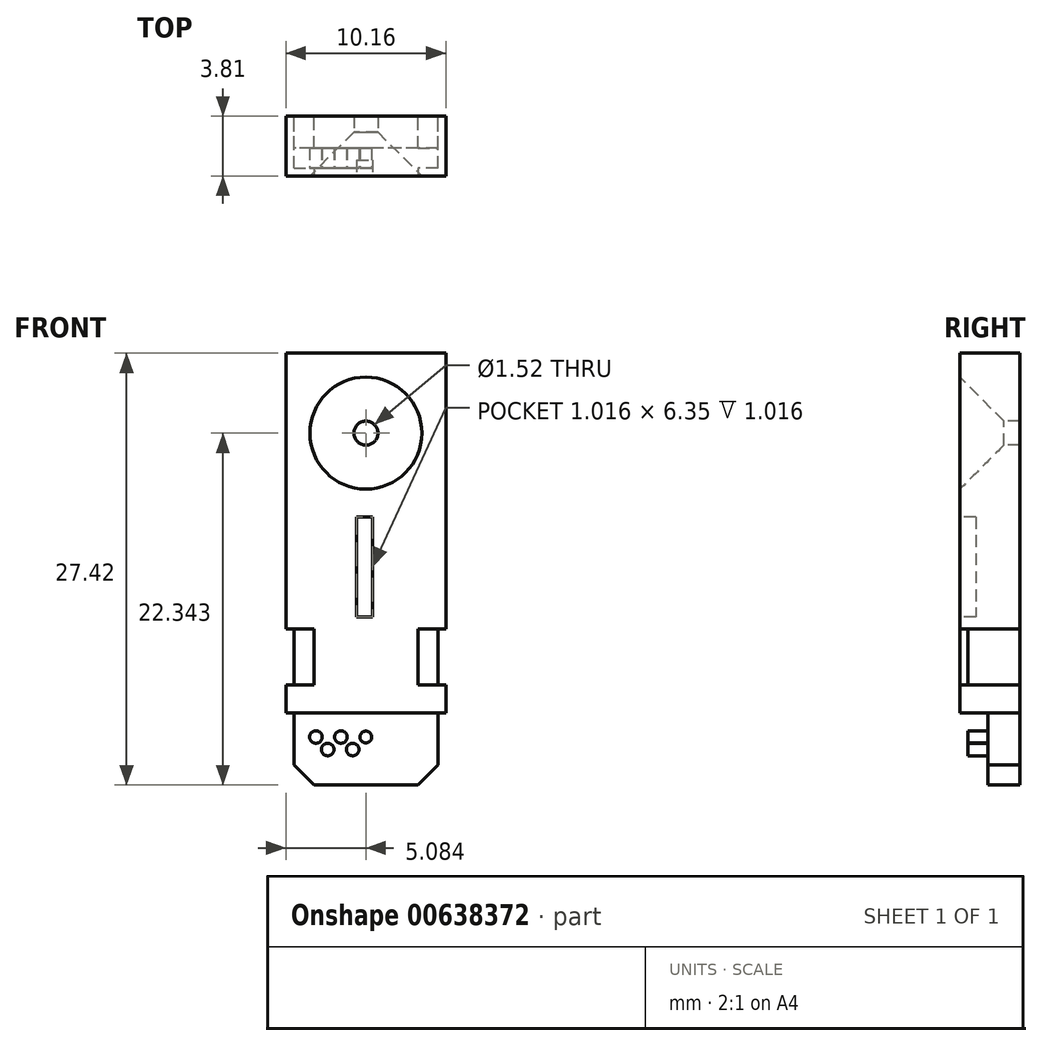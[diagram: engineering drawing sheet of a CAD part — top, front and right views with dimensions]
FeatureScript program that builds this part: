
annotation { "Feature Type Name" : "Feature", "Feature Type Description" : "" }
export const myFeature = defineFeature(function(context is Context, id is Id, definition is map)
    precondition{}
    {
        {
            var Q0;
            Q0=qCreatedBy(makeId("Front.planeOp"),FACE);
            var sketch = newSketch(context, id + "F0", { "sketchPlane" : qUnion([Q0])});
            skLineSegment(sketch, "E0", {"start": v(11.18, 15.01) * mm, "end": v(21.34, 15.01) * mm});
            skLineSegment(sketch, "E1", {"start": v(21.34, 15.01) * mm, "end": v(21.34, -7.85) * mm});
            skLineSegment(sketch, "E2", {"start": v(21.34, -7.85) * mm, "end": v(20.84, -7.85) * mm});
            skLineSegment(sketch, "E3", {"start": v(11.18, -7.85) * mm, "end": v(11.18, 15.01) * mm});
            skLineSegment(sketch, "E4", {"start": v(11.18, -7.85) * mm, "end": v(11.7, -7.85) * mm});
            skLineSegment(sketch, "E5", {"start": v(11.7, -7.85) * mm, "end": v(11.7, -11.14) * mm});
            skLineSegment(sketch, "E6", {"start": v(12.96, -12.41) * mm, "end": v(11.7, -11.14) * mm});
            skLineSegment(sketch, "E7", {"start": v(20.84, -7.85) * mm, "end": v(20.84, -11.14) * mm});
            skLineSegment(sketch, "E8", {"start": v(19.57, -12.41) * mm, "end": v(20.84, -11.14) * mm});
            skLineSegment(sketch, "E9", {"start": v(19.57, -12.41) * mm, "end": v(12.96, -12.41) * mm});
            skLineSegment(sketch, "E10", {"start": v(11.7, -7.85) * mm, "end": v(11.18, -7.85) * mm});
            skLineSegment(sketch, "E11", {"start": v(20.84, -7.85) * mm, "end": v(11.7, -7.85) * mm});
            skSolve(sketch);
        }
        {
            var Q0;
            Q0=makeQuery(id+"F0.imprint","IMPRINT",FACE,{"disambiguationData":[TD([[makeQuery(id+"F0.imprint","IMPRINT",EDGE,{"derivedFrom":sQuery(id+"F0.wireOp",EDGE,"E0")}),-1.0]])]});
            extrude(context, id + "F1", {"entities" : qUnion([Q0]), "depth" : 3.8 * mm, "offsetDistance" : 25.4 * mm});
        }
        {
            var Q0;
            Q0=makeQuery(id+"F0.imprint","IMPRINT",FACE,{"disambiguationData":[TD([[makeQuery(id+"F0.imprint","IMPRINT",EDGE,{"derivedFrom":sQuery(id+"F0.wireOp",EDGE,"E5")}),1.0]])]});
            extrude(context, id + "F2", {"entities" : qUnion([Q0]), "operationType" : NewBodyOperationType.ADD, "depth" : 3.3 * mm, "offsetDistance" : 25.4 * mm});
        }
        {
            var Q0;
            Q0=makeQuery(id+"F1.opExtrude","CAP_FACE",FACE,{"disambiguationData":[OSD([sQuery(id+"F0.wireOp",EDGE,"E0"),sQuery(id+"F0.wireOp",EDGE,"E1"),sQuery(id+"F0.wireOp",EDGE,"E3"),sQuery(id+"F0.wireOp",EDGE,"E2"),sQuery(id+"F0.wireOp",EDGE,"E10"),sQuery(id+"F0.wireOp",EDGE,"E11")])],"isStart":false});
            var sketch = newSketch(context, id + "F3", { "sketchPlane" : qUnion([Q0])});
            skLineSegment(sketch, "E12", {"start": v(16.26, 15.01) * mm, "end": v(16.26, 9.93) * mm});
            skPoint(sketch, "E12.endSnap0", {"position": v(16.26, 15.01) * mm});
            skSolve(sketch);
        }
        {
            var Q0;
            Q0=sQuery(id+"F3.wireOp",VERTEX,"E12.end");
            var Q1;
            Q1=makeQuery(id+"F1.opExtrude","SWEPT_BODY",BODY,{"disambiguationData":[OSD([sQuery(id+"F0.wireOp",EDGE,"E0"),sQuery(id+"F0.wireOp",EDGE,"E1"),sQuery(id+"F0.wireOp",EDGE,"E3"),sQuery(id+"F0.wireOp",EDGE,"E2"),sQuery(id+"F0.wireOp",EDGE,"E10"),sQuery(id+"F0.wireOp",EDGE,"E11")])]});
            hole(context, id + "F4", {"style" : HoleStyle.C_SINK, "endStyle" : HoleEndStyle.THROUGH, "holeDiameter" : 1.52 * mm, "cSinkDiameter" : 7.11 * mm, "cSinkAngle" : 90 * degree, "majorDiameter" : 6.35 * mm, "isTappedThrough" : true, "tappedDepth" : 12.7 * mm, "tapClearance" : 3, "startFromSketch" : true, "locations" : qUnion([Q0]), "scope" : qUnion([Q1])});
        }
        {
            var Q0;
            Q0=makeQuery(id+"F1.opExtrude","CAP_FACE",FACE,{"disambiguationData":[OSD([sQuery(id+"F0.wireOp",EDGE,"E0"),sQuery(id+"F0.wireOp",EDGE,"E1"),sQuery(id+"F0.wireOp",EDGE,"E3"),sQuery(id+"F0.wireOp",EDGE,"E2"),sQuery(id+"F0.wireOp",EDGE,"E10"),sQuery(id+"F0.wireOp",EDGE,"E11")])],"isStart":false});
            var sketch = newSketch(context, id + "F5", { "sketchPlane" : qUnion([Q0])});
            skLineSegment(sketch, "E13", {"start": v(16.19, 4.6) * mm, "end": v(16.7, 4.6) * mm});
            skLineSegment(sketch, "E14", {"start": v(16.7, 4.6) * mm, "end": v(15.68, 4.6) * mm});
            skLineSegment(sketch, "E15", {"start": v(15.68, 4.6) * mm, "end": v(15.68, -1.75) * mm});
            skLineSegment(sketch, "E16", {"start": v(15.68, -1.75) * mm, "end": v(16.7, -1.75) * mm});
            skLineSegment(sketch, "E17", {"start": v(16.7, -1.75) * mm, "end": v(16.7, 4.6) * mm});
            skSolve(sketch);
        }
        {
            var Q0;
            {var subQ0=sQuery(id+"F5.wireOp",EDGE,"E15");Q0=makeQuery(id+"F5.imprint","IMPRINT",FACE,{"disambiguationData":[TD([[makeQuery(id+"F5.imprint","IMPRINT",EDGE,{"derivedFrom":subQ0}),1.0]])]});}
            extrude(context, id + "F6", {"entities" : qUnion([Q0]), "operationType" : NewBodyOperationType.REMOVE, "oppositeDirection" : true, "depth" : 1.02 * mm, "offsetDistance" : 25.4 * mm});
        }
        {
            var Q0;
            Q0=makeQuery(id+"F1.opExtrude","CAP_FACE",FACE,{"disambiguationData":[OSD([sQuery(id+"F0.wireOp",EDGE,"E0"),sQuery(id+"F0.wireOp",EDGE,"E1"),sQuery(id+"F0.wireOp",EDGE,"E3"),sQuery(id+"F0.wireOp",EDGE,"E2"),sQuery(id+"F0.wireOp",EDGE,"E10"),sQuery(id+"F0.wireOp",EDGE,"E11")])],"isStart":false});
            var sketch = newSketch(context, id + "F7", { "sketchPlane" : qUnion([Q0])});
            skLineSegment(sketch, "E18", {"start": v(11.18, -7.85) * mm, "end": v(11.18, -6.07) * mm});
            skLineSegment(sketch, "E19", {"start": v(11.18, -6.07) * mm, "end": v(12.96, -6.07) * mm});
            skLineSegment(sketch, "E20", {"start": v(12.96, -6.07) * mm, "end": v(12.96, -2.51) * mm});
            skLineSegment(sketch, "E21", {"start": v(12.96, -2.51) * mm, "end": v(11.18, -2.51) * mm});
            skLineSegment(sketch, "E22", {"start": v(21.34, -6.07) * mm, "end": v(19.57, -6.07) * mm});
            skLineSegment(sketch, "E23", {"start": v(19.57, -6.07) * mm, "end": v(19.57, -2.51) * mm});
            skLineSegment(sketch, "E24", {"start": v(19.57, -2.51) * mm, "end": v(21.34, -2.51) * mm});
            skSolve(sketch);
        }
        {
            var Q0;
            {var subQ0=sQuery(id+"F7.wireOp",EDGE,"E19");Q0=makeQuery(id+"F7.imprint","IMPRINT",FACE,{"disambiguationData":[TD([[makeQuery(id+"F7.imprint","IMPRINT",EDGE,{"derivedFrom":subQ0}),1.0]])]});}
            var Q1;
            {var subQ0=sQuery(id+"F7.wireOp",EDGE,"E22");Q1=makeQuery(id+"F7.imprint","IMPRINT",FACE,{"disambiguationData":[TD([[makeQuery(id+"F7.imprint","IMPRINT",EDGE,{"derivedFrom":subQ0}),-1.0]])]});}
            extrude(context, id + "F8", {"entities" : qUnion([Q0, Q1]), "operationType" : NewBodyOperationType.REMOVE, "oppositeDirection" : true, "depth" : 0.5 * mm, "offsetDistance" : 25.4 * mm});
        }
        {
            var Q0;
            Q0=makeQuery(id+"F1.opExtrude","SWEPT_FACE",FACE,{"disambiguationData":[OSD([sQuery(id+"F0.wireOp",EDGE,"E1")])]});
            var sketch = newSketch(context, id + "F9", { "sketchPlane" : qUnion([Q0])});
            skLineSegment(sketch, "E25", {"start": v(-3.3, -2.51) * mm, "end": v(0, -2.51) * mm});
            skLineSegment(sketch, "E26", {"start": v(-3.3, -6.07) * mm, "end": v(0, -6.07) * mm});
            skSolve(sketch);
        }
        {
            var Q0;
            {var subQ0=sQuery(id+"F9.wireOp",EDGE,"E25");Q0=makeQuery(id+"F9.imprint","IMPRINT",FACE,{"disambiguationData":[TD([[makeQuery(id+"F9.imprint","IMPRINT",EDGE,{"derivedFrom":subQ0}),-1.0]])]});}
            extrude(context, id + "F10", {"entities" : qUnion([Q0]), "operationType" : NewBodyOperationType.REMOVE, "oppositeDirection" : true, "depth" : 0.5 * mm, "offsetDistance" : 25.4 * mm});
        }
        {
            var Q0;
            Q0=makeQuery(id+"F1.opExtrude","SWEPT_FACE",FACE,{"disambiguationData":[OSD([sQuery(id+"F0.wireOp",EDGE,"E3")])]});
            var sketch = newSketch(context, id + "F11", { "sketchPlane" : qUnion([Q0])});
            skLineSegment(sketch, "E27", {"start": v(3.3, -2.51) * mm, "end": v(0, -2.51) * mm});
            skLineSegment(sketch, "E28", {"start": v(3.3, -6.07) * mm, "end": v(0, -6.07) * mm});
            skSolve(sketch);
        }
        {
            var Q0;
            {var subQ0=sQuery(id+"F11.wireOp",EDGE,"E27");Q0=makeQuery(id+"F11.imprint","IMPRINT",FACE,{"disambiguationData":[TD([[makeQuery(id+"F11.imprint","IMPRINT",EDGE,{"derivedFrom":subQ0}),1.0]])]});}
            extrude(context, id + "F12", {"entities" : qUnion([Q0]), "operationType" : NewBodyOperationType.REMOVE, "oppositeDirection" : true, "depth" : 0.5 * mm, "offsetDistance" : 25.4 * mm});
        }
        {
            var Q0;
            Q0=makeQuery(id+"F2.opExtrude","CAP_FACE",FACE,{"disambiguationData":[OSD([sQuery(id+"F0.wireOp",EDGE,"E5"),sQuery(id+"F0.wireOp",EDGE,"E6"),sQuery(id+"F0.wireOp",EDGE,"E7"),sQuery(id+"F0.wireOp",EDGE,"E8"),sQuery(id+"F0.wireOp",EDGE,"E9"),sQuery(id+"F0.wireOp",EDGE,"E11")])],"isStart":false});
            var sketch = newSketch(context, id + "F13", { "sketchPlane" : qUnion([Q0])});
            skCircle(sketch, "E29", {"center": v(16.26, -9.37) * mm, "radius": 0.37 * mm});
            skCircle(sketch, "E30", {"center": v(17.1, -10.17) * mm, "radius": 0.4 * mm});
            skCircle(sketch, "E31", {"center": v(17.85, -9.37) * mm, "radius": 0.4 * mm});
            skCircle(sketch, "E32", {"center": v(18.69, -10.17) * mm, "radius": 0.4 * mm});
            skCircle(sketch, "E33", {"center": v(19.44, -9.37) * mm, "radius": 0.4 * mm});
            skCircle(sketch, "E34.MirrorC", {"center": v(15.43, -10.17) * mm, "radius": 0.4 * mm});
            skCircle(sketch, "E35.MirrorC", {"center": v(14.68, -9.37) * mm, "radius": 0.4 * mm});
            skCircle(sketch, "E36.MirrorC", {"center": v(13.84, -10.17) * mm, "radius": 0.4 * mm});
            skCircle(sketch, "E37.MirrorC", {"center": v(13.09, -9.37) * mm, "radius": 0.4 * mm});
            skSolve(sketch);
        }
        {
            var Q0;
            Q0=makeQuery(id+"F13.imprint","IMPRINT",FACE,{"disambiguationData":[TD([[makeQuery(id+"F13.imprint","IMPRINT",EDGE,{"derivedFrom":sQuery(id+"F13.wireOp",EDGE,"E37.MirrorC")}),-1.0]])]});
            var Q1;
            Q1=makeQuery(id+"F13.imprint","IMPRINT",FACE,{"disambiguationData":[TD([[makeQuery(id+"F13.imprint","IMPRINT",EDGE,{"derivedFrom":sQuery(id+"F13.wireOp",EDGE,"E35.MirrorC")}),-1.0]])]});
            var Q2;
            Q2=makeQuery(id+"F13.imprint","IMPRINT",FACE,{"disambiguationData":[TD([[makeQuery(id+"F13.imprint","IMPRINT",EDGE,{"derivedFrom":sQuery(id+"F13.wireOp",EDGE,"E36.MirrorC")}),-1.0]])]});
            var Q3;
            Q3=makeQuery(id+"F13.imprint","IMPRINT",FACE,{"disambiguationData":[TD([[makeQuery(id+"F13.imprint","IMPRINT",EDGE,{"derivedFrom":sQuery(id+"F13.wireOp",EDGE,"E34.MirrorC")}),-1.0]])]});
            var Q4;
            Q4=makeQuery(id+"F13.imprint","IMPRINT",FACE,{"disambiguationData":[TD([[makeQuery(id+"F13.imprint","IMPRINT",EDGE,{"derivedFrom":sQuery(id+"F13.wireOp",EDGE,"E29")}),-1.0]])]});
            var Q5;
            Q5=makeQuery(id+"F13.imprint","IMPRINT",FACE,{"disambiguationData":[TD([[makeQuery(id+"F13.imprint","IMPRINT",EDGE,{"derivedFrom":sQuery(id+"F13.wireOp",EDGE,"E30")}),1.0]])]});
            var Q6;
            Q6=makeQuery(id+"F13.imprint","IMPRINT",FACE,{"disambiguationData":[TD([[makeQuery(id+"F13.imprint","IMPRINT",EDGE,{"derivedFrom":sQuery(id+"F13.wireOp",EDGE,"E31")}),1.0]])]});
            var Q7;
            Q7=makeQuery(id+"F13.imprint","IMPRINT",FACE,{"disambiguationData":[TD([[makeQuery(id+"F13.imprint","IMPRINT",EDGE,{"derivedFrom":sQuery(id+"F13.wireOp",EDGE,"E32")}),1.0]])]});
            var Q8;
            Q8=makeQuery(id+"F13.imprint","IMPRINT",FACE,{"disambiguationData":[TD([[makeQuery(id+"F13.imprint","IMPRINT",EDGE,{"derivedFrom":sQuery(id+"F13.wireOp",EDGE,"E33")}),1.0]])]});
            extrude(context, id + "F14", {"entities" : qUnion([Q0, Q1, Q2, Q3, Q4, Q5, Q6, Q7, Q8]), "operationType" : NewBodyOperationType.REMOVE, "oppositeDirection" : true, "depth" : 1.27 * mm, "offsetDistance" : 25.4 * mm});
        }
    });
